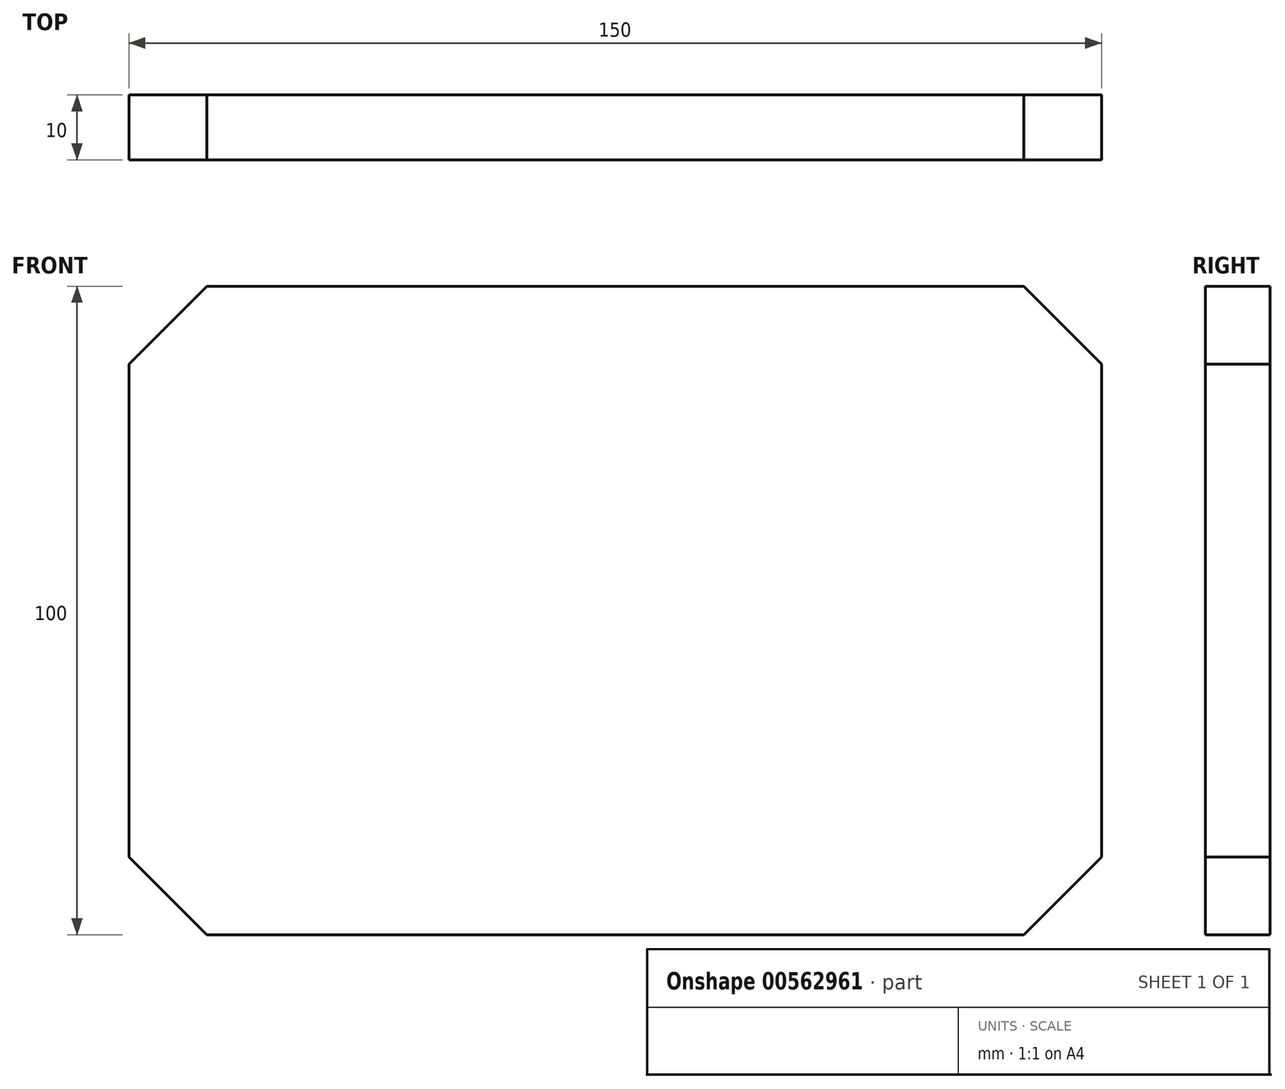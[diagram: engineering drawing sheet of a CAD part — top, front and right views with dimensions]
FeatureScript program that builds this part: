
annotation { "Feature Type Name" : "Feature", "Feature Type Description" : "" }
export const myFeature = defineFeature(function(context is Context, id is Id, definition is map)
    precondition{}
    {
        {
            var Q0;
            Q0=qCreatedBy(makeId("Front.planeOp"),FACE);
            var sketch = newSketch(context, id + "F0", { "sketchPlane" : qUnion([Q0])});
            skLineSegment(sketch, "E0.bottom", {"start": v(75, 50) * mm, "end": v(-75, 50) * mm});
            skLineSegment(sketch, "E0.top", {"start": v(75, -50) * mm, "end": v(-75, -50) * mm});
            skLineSegment(sketch, "E0.left", {"start": v(75, 50) * mm, "end": v(75, -50) * mm});
            skLineSegment(sketch, "E0.right", {"start": v(-75, 50) * mm, "end": v(-75, -50) * mm});
            skPoint(sketch, "E0.middle", {"position": v(0, 0) * mm});
            skSolve(sketch);
        }
        {
            var Q0;
            Q0=makeQuery(id+"F0.imprint","IMPRINT",FACE,{"disambiguationData":[TD([[makeQuery(id+"F0.imprint","IMPRINT",EDGE,{"derivedFrom":sQuery(id+"F0.wireOp",EDGE,"E0.bottom")}),1.0]])]});
            extrude(context, id + "F1", {"entities" : qUnion([Q0]), "depth" : 10 * mm, "offsetDistance" : 25 * mm});
        }
        {
            var Q0;
            Q0=makeQuery(id+"F1.opExtrude","SWEPT_EDGE",EDGE,{"disambiguationData":[OSD([sQuery(id+"F0.wireOp",EDGE,"E0.top"),sQuery(id+"F0.wireOp",EDGE,"E0.left")])]});
            var Q1;
            Q1=makeQuery(id+"F1.opExtrude","SWEPT_EDGE",EDGE,{"disambiguationData":[OSD([sQuery(id+"F0.wireOp",EDGE,"E0.bottom"),sQuery(id+"F0.wireOp",EDGE,"E0.left")])]});
            var Q2;
            Q2=makeQuery(id+"F1.opExtrude","SWEPT_EDGE",EDGE,{"disambiguationData":[OSD([sQuery(id+"F0.wireOp",EDGE,"E0.top"),sQuery(id+"F0.wireOp",EDGE,"E0.right")])]});
            var Q3;
            Q3=makeQuery(id+"F1.opExtrude","SWEPT_EDGE",EDGE,{"disambiguationData":[OSD([sQuery(id+"F0.wireOp",EDGE,"E0.bottom"),sQuery(id+"F0.wireOp",EDGE,"E0.right")])]});
            chamfer(context, id + "F2", {"entities" : qUnion([Q0, Q1, Q2, Q3]), "width" : 12 * mm, "tangentPropagation" : true});
        }
    });
